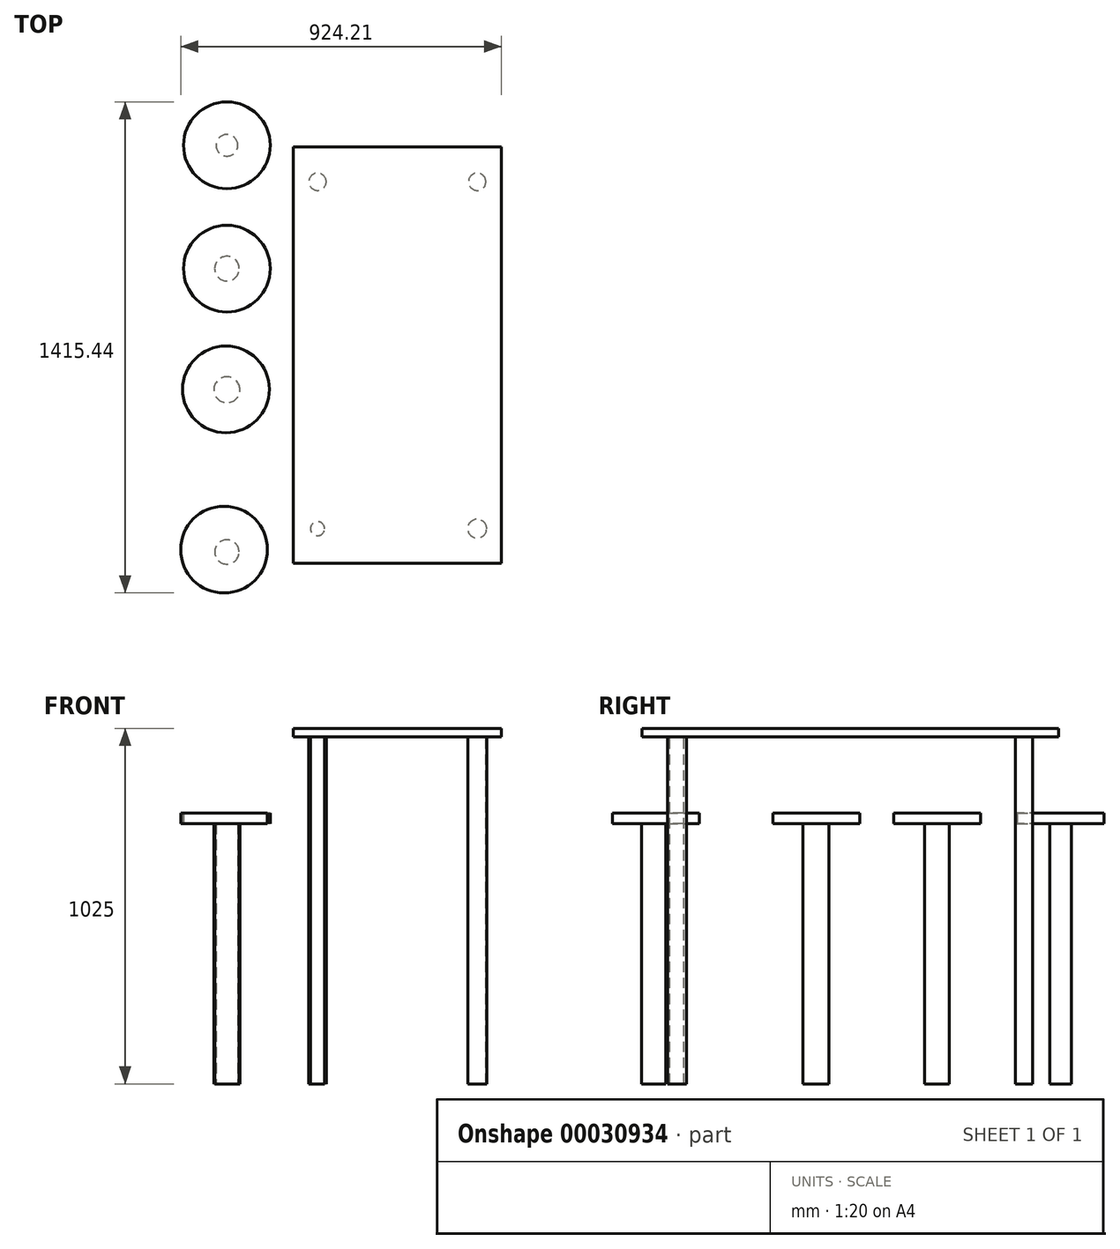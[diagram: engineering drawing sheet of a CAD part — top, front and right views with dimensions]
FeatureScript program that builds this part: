
annotation { "Feature Type Name" : "Feature", "Feature Type Description" : "" }
export const myFeature = defineFeature(function(context is Context, id is Id, definition is map)
    precondition{}
    {
        {
            var Q0;
            Q0=qCreatedBy(makeId("Top.planeOp"),FACE);
            var sketch = newSketch(context, id + "F0", { "sketchPlane" : qUnion([Q0])});
            skLineSegment(sketch, "E0.bottom", {"start": v(0, 0) * mm, "end": v(-600, 0) * mm});
            skLineSegment(sketch, "E0.top", {"start": v(0, 1200) * mm, "end": v(-600, 1200) * mm});
            skLineSegment(sketch, "E0.left", {"start": v(0, 0) * mm, "end": v(0, 1200) * mm});
            skLineSegment(sketch, "E0.right", {"start": v(-600, 0) * mm, "end": v(-600, 1200) * mm});
            skSolve(sketch);
        }
        {
            var Q0;
            Q0=makeQuery(id+"F0.imprint","IMPRINT",FACE,{"disambiguationData":[TD([[makeQuery(id+"F0.imprint","IMPRINT",EDGE,{"derivedFrom":sQuery(id+"F0.wireOp",EDGE,"E0.bottom")}),-1.0]])]});
            var sketch = newSketch(context, id + "F1", { "sketchPlane" : qUnion([Q0])});
            skCircle(sketch, "E1", {"center": v(-530, 1100) * mm, "radius": 25 * mm});
            skCircle(sketch, "E2", {"center": v(-70, 1100) * mm, "radius": 25.05 * mm});
            skCircle(sketch, "E3", {"center": v(-70, 100) * mm, "radius": 27.28 * mm});
            skCircle(sketch, "E4", {"center": v(-530, 100) * mm, "radius": 20.36 * mm});
            skSolve(sketch);
        }
        {
            var Q0;
            Q0 = qSketchRegion(id + "F1", true);
            extrude(context, id + "F2", {"entities" : qUnion([Q0]), "oppositeDirection" : true, "depth" : 1000 * mm});
        }
        {
            var Q0;
            Q0=makeQuery(id+"F0.imprint","IMPRINT",FACE,{"disambiguationData":[TD([[makeQuery(id+"F0.imprint","IMPRINT",EDGE,{"derivedFrom":sQuery(id+"F0.wireOp",EDGE,"E0.bottom")}),-1.0]])]});
            extrude(context, id + "F3", {"entities" : qUnion([Q0]), "depth" : 25 * mm});
        }
        {
            var Q0;
            Q0=makeQuery(id+"F2.opExtrude","CAP_FACE",FACE,{"disambiguationData":[OSD([sQuery(id+"F1.wireOp",EDGE,"E4")])],"isStart":false});
            var sketch = newSketch(context, id + "F4", { "sketchPlane" : qUnion([Q0])});
            skCircle(sketch, "E5", {"center": v(-791.02, -32.98) * mm, "radius": 35 * mm});
            skCircle(sketch, "E6", {"center": v(-791.02, -500.52) * mm, "radius": 37.54 * mm});
            skCircle(sketch, "E7", {"center": v(-791.02, -849.53) * mm, "radius": 35.61 * mm});
            skCircle(sketch, "E8", {"center": v(-791.02, -1205.12) * mm, "radius": 31.24 * mm});
            skSolve(sketch);
        }
        {
            var Q0;
            Q0 = qSketchRegion(id + "F4", true);
            extrude(context, id + "F5", {"entities" : qUnion([Q0]), "oppositeDirection" : true, "depth" : 750 * mm});
        }
        {
            var Q0;
            Q0=makeQuery(id+"F5.opExtrude","CAP_FACE",FACE,{"disambiguationData":[OSD([sQuery(id+"F4.wireOp",EDGE,"E8")])],"isStart":false});
            var sketch = newSketch(context, id + "F6", { "sketchPlane" : qUnion([Q0])});
            skCircle(sketch, "E9", {"center": v(-791.02, 1205.12) * mm, "radius": 125 * mm});
            skSolve(sketch);
        }
        {
            var Q0;
            Q0 = qSketchRegion(id + "F6", true);
            extrude(context, id + "F7", {"entities" : qUnion([Q0]), "operationType" : NewBodyOperationType.ADD, "depth" : 30 * mm});
        }
        {
            var Q0;
            Q0=makeQuery(id+"F5.opExtrude","CAP_FACE",FACE,{"disambiguationData":[OSD([sQuery(id+"F4.wireOp",EDGE,"E7")])],"isStart":false});
            var sketch = newSketch(context, id + "F8", { "sketchPlane" : qUnion([Q0])});
            skCircle(sketch, "E10", {"center": v(-791.02, 849.53) * mm, "radius": 125 * mm});
            skCircle(sketch, "E11", {"center": v(-793.87, 501.48) * mm, "radius": 125 * mm});
            skCircle(sketch, "E12", {"center": v(-799.21, 39.68) * mm, "radius": 125 * mm});
            skSolve(sketch);
        }
        {
            var Q0;
            Q0 = qSketchRegion(id + "F8", true);
            extrude(context, id + "F9", {"entities" : qUnion([Q0]), "depth" : 30 * mm});
        }
    });
